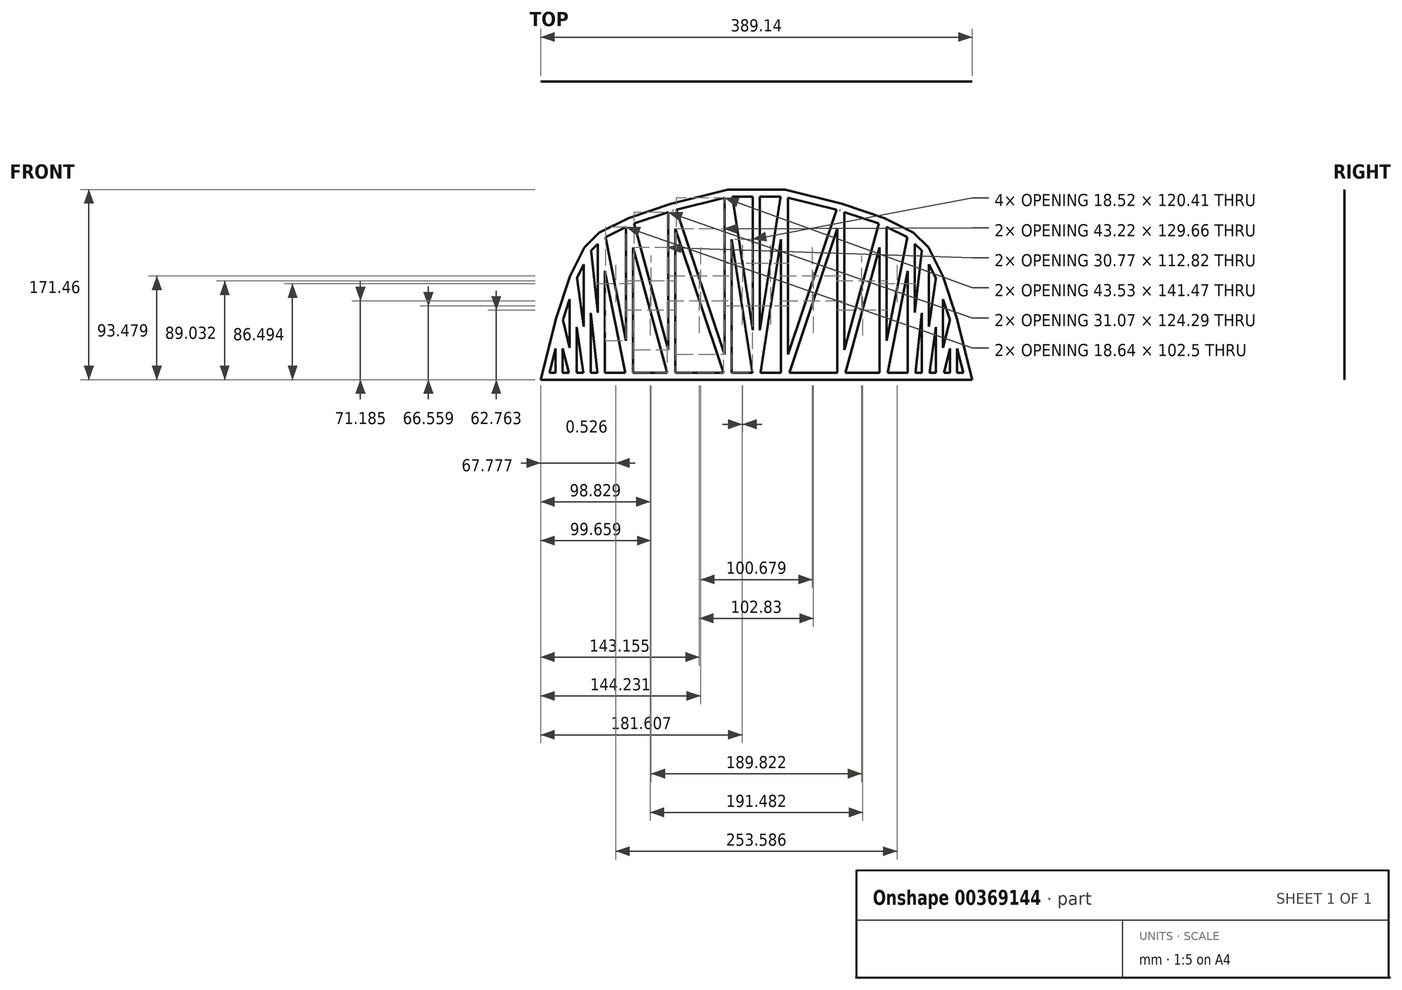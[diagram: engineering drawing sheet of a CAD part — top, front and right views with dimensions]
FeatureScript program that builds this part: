
annotation { "Feature Type Name" : "Feature", "Feature Type Description" : "" }
export const myFeature = defineFeature(function(context is Context, id is Id, definition is map)
    precondition{}
    {
        {
            var Q0;
            Q0=qCreatedBy(makeId("Front.planeOp"),FACE);
            var sketch = newSketch(context, id + "F0", { "sketchPlane" : qUnion([Q0])});
            skLineSegment(sketch, "E0", {"start": v(0, 0) * mm, "end": v(0, 165.1) * mm});
            skLineSegment(sketch, "E1", {"start": v(-75.2, 149.39) * mm, "end": v(-75.2, 149.38) * mm});
            skLineSegment(sketch, "E2", {"start": v(-193.77, 0) * mm, "end": v(-180.85, 51.69) * mm});
            skLineSegment(sketch, "E3", {"start": v(-180.85, 51.69) * mm, "end": v(-168.04, 90.12) * mm});
            skLineSegment(sketch, "E4", {"start": v(-168.04, 90.12) * mm, "end": v(-155, 116.18) * mm});
            skLineSegment(sketch, "E5", {"start": v(-155, 116.18) * mm, "end": v(-141.58, 129.6) * mm});
            skLineSegment(sketch, "E6", {"start": v(-141.58, 129.6) * mm, "end": v(-119.91, 140.44) * mm});
            skLineSegment(sketch, "E7", {"start": v(-115.52, 142.64) * mm, "end": v(-77.04, 155.47) * mm});
            skLineSegment(sketch, "E8", {"start": v(-77.09, 155.45) * mm, "end": v(-30.66, 167.06) * mm});
            skLineSegment(sketch, "E9", {"start": v(-25.8, 168.28) * mm, "end": v(0, 168.28) * mm});
            skPoint(sketch, "E10", {"position": v(-180.85, 51.69) * mm});
            skPoint(sketch, "E11", {"position": v(-168.04, 90.12) * mm});
            skPoint(sketch, "E12", {"position": v(-155, 116.18) * mm});
            skPoint(sketch, "E13", {"position": v(-141.58, 129.6) * mm});
            skLineSegment(sketch, "E14", {"start": v(-119.91, 140.44) * mm, "end": v(-115.52, 142.64) * mm});
            skPoint(sketch, "E15", {"position": v(-115.52, 142.64) * mm});
            skPoint(sketch, "E16.orphan", {"position": v(-122.1, 140.44) * mm});
            skLineSegment(sketch, "E17", {"start": v(-30.66, 167.06) * mm, "end": v(-25.8, 168.28) * mm});
            skLineSegment(sketch, "E18", {"start": v(-186.43, 3.17) * mm, "end": v(-180.97, 25) * mm});
            skLineSegment(sketch, "E19", {"start": v(-174.75, 49.91) * mm, "end": v(-168.27, 69.33) * mm});
            skPoint(sketch, "E20", {"position": v(-149.8, 112.42) * mm});
            skLineSegment(sketch, "E21.trimOffspring", {"start": v(-149.08, 113.13) * mm, "end": v(-142.88, 119.33) * mm});
            skPoint(sketch, "E22", {"position": v(-162.16, 87.68) * mm});
            skLineSegment(sketch, "E23.trimOffspring", {"start": v(-162.16, 87.68) * mm, "end": v(-155.57, 100.85) * mm});
            skPoint(sketch, "E24", {"position": v(-174.75, 49.91) * mm});
            skLineSegment(sketch, "E25", {"start": v(-136.11, 125.24) * mm, "end": v(-117.48, 134.56) * mm});
            skLineSegment(sketch, "E26", {"start": v(-110.45, 137.64) * mm, "end": v(-79.38, 148) * mm});
            skLineSegment(sketch, "E27", {"start": v(-75.31, 149.35) * mm, "end": v(-75.2, 149.38) * mm});
            skLineSegment(sketch, "E28", {"start": v(-3.17, 161.93) * mm, "end": v(-21.7, 161.93) * mm});
            skPoint(sketch, "E29", {"position": v(-137.82, 124.4) * mm});
            skPoint(sketch, "E30", {"position": v(-113.08, 136.76) * mm});
            skPoint(sketch, "E31", {"position": v(-75.31, 149.35) * mm});
            skPoint(sketch, "E32", {"position": v(-25, 161.92) * mm});
            skLineSegment(sketch, "E33", {"start": v(0, 165.1) * mm, "end": v(0, 168.28) * mm});
            skLineSegment(sketch, "E34", {"start": v(-186.43, 3.17) * mm, "end": v(-180.98, 3.17) * mm});
            skLineSegment(sketch, "E35", {"start": v(0, 0) * mm, "end": v(0, -3.18) * mm});
            skLineSegment(sketch, "E36", {"start": v(0, -3.18) * mm, "end": v(-194.57, -3.18) * mm});
            skLineSegment(sketch, "E37", {"start": v(-193.77, 0) * mm, "end": v(-194.57, -3.18) * mm});
            skLineSegment(sketch, "E38", {"start": v(-180.98, 3.17) * mm, "end": v(-180.98, 25) * mm});
            skLineSegment(sketch, "E39", {"start": v(-174.63, 3.17) * mm, "end": v(-174.63, 25) * mm});
            skLineSegment(sketch, "E40", {"start": v(-168.27, 25.8) * mm, "end": v(-174.5, 50.67) * mm});
            skLineSegment(sketch, "E41", {"start": v(-169.17, 3.17) * mm, "end": v(-174.63, 25) * mm});
            skLineSegment(sketch, "E42", {"start": v(-168.27, 25.8) * mm, "end": v(-168.27, 69.33) * mm});
            skLineSegment(sketch, "E43", {"start": v(-155.57, 44.68) * mm, "end": v(-155.57, 100.85) * mm});
            skLineSegment(sketch, "E44", {"start": v(-155.57, 44.68) * mm, "end": v(-161.82, 88.37) * mm});
            skLineSegment(sketch, "E45", {"start": v(-161.93, 44.22) * mm, "end": v(-156.06, 3.17) * mm});
            skLineSegment(sketch, "E46", {"start": v(-142.88, 57.33) * mm, "end": v(-142.88, 119.33) * mm});
            skLineSegment(sketch, "E47", {"start": v(-136.53, 94.94) * mm, "end": v(-136.53, 3.17) * mm});
            skLineSegment(sketch, "E48", {"start": v(-142.87, 57.33) * mm, "end": v(-149.08, 113.13) * mm});
            skLineSegment(sketch, "E49", {"start": v(-142.88, -0.18) * mm, "end": v(-142.9, 0) * mm});
            skLineSegment(sketch, "E50", {"start": v(-117.48, 134.56) * mm, "end": v(-117.48, 32.06) * mm});
            skLineSegment(sketch, "E51", {"start": v(-111.13, 3.17) * mm, "end": v(-111.13, 116) * mm});
            skLineSegment(sketch, "E52", {"start": v(-136.11, 125.24) * mm, "end": v(-117.48, 32.06) * mm});
            skLineSegment(sketch, "E53", {"start": v(-136.52, 94.94) * mm, "end": v(-118.17, 3.17) * mm});
            skLineSegment(sketch, "E54", {"start": v(-73.03, 132.83) * mm, "end": v(-73.03, 3.17) * mm});
            skLineSegment(sketch, "E55", {"start": v(-110.45, 137.64) * mm, "end": v(-79.38, 23.7) * mm});
            skLineSegment(sketch, "E56", {"start": v(-111.13, 116) * mm, "end": v(-80.36, 3.17) * mm});
            skLineSegment(sketch, "E57", {"start": v(-22.23, 3.17) * mm, "end": v(-22.23, 123.58) * mm});
            skLineSegment(sketch, "E58", {"start": v(-28.58, 161.03) * mm, "end": v(-28.58, 19.57) * mm});
            skLineSegment(sketch, "E59", {"start": v(-72.1, 150.15) * mm, "end": v(-28.57, 19.57) * mm});
            skLineSegment(sketch, "E60", {"start": v(-29.8, 3.17) * mm, "end": v(-73.03, 132.83) * mm});
            skLineSegment(sketch, "E61", {"start": v(-3.18, 161.93) * mm, "end": v(-3.17, 41.52) * mm});
            skLineSegment(sketch, "E62", {"start": v(-3.17, 41.52) * mm, "end": v(-21.7, 161.93) * mm});
            skLineSegment(sketch, "E63", {"start": v(-22.23, 123.58) * mm, "end": v(-3.7, 3.17) * mm});
            skLineSegment(sketch, "E64.trimOffspring", {"start": v(-143.25, 3.17) * mm, "end": v(-149.23, 56.97) * mm});
            skPoint(sketch, "E65.orphan", {"position": v(-139.7, 0) * mm});
            skPoint(sketch, "E66.orphan", {"position": v(-114.3, 0) * mm});
            skPoint(sketch, "E67.orphan", {"position": v(-149, 114.02) * mm});
            skPoint(sketch, "E68.start.orphan", {"position": v(-139.7, 127) * mm});
            skPoint(sketch, "E69.start.orphan", {"position": v(-114.3, 139.7) * mm});
            skLineSegment(sketch, "E70.trimOffspring", {"start": v(-174.63, 3.17) * mm, "end": v(-169.17, 3.17) * mm});
            skLineSegment(sketch, "E71.trimOffspring", {"start": v(-161.93, 3.17) * mm, "end": v(-156.06, 3.17) * mm});
            skLineSegment(sketch, "E72.trimOffspring", {"start": v(-161.93, 44.22) * mm, "end": v(-161.93, 3.17) * mm});
            skLineSegment(sketch, "E73.trimOffspring", {"start": v(-149.23, 3.17) * mm, "end": v(-143.25, 3.17) * mm});
            skLineSegment(sketch, "E74.trimOffspring", {"start": v(-149.23, 56.97) * mm, "end": v(-149.23, 3.17) * mm});
            skLineSegment(sketch, "E75.trimOffspring", {"start": v(-79.38, 23.7) * mm, "end": v(-79.38, 148) * mm});
            skPoint(sketch, "E76.end.orphan", {"position": v(-114.3, 127) * mm});
            skLineSegment(sketch, "E77.trimOffspring", {"start": v(-72.1, 150.15) * mm, "end": v(-28.58, 161.03) * mm});
            skLineSegment(sketch, "E78.trimOffspring", {"start": v(-75.31, 149.35) * mm, "end": v(-75.2, 149.39) * mm});
            skLineSegment(sketch, "E79.trimOffspring", {"start": v(-22.23, 3.17) * mm, "end": v(-3.7, 3.17) * mm});
            skLineSegment(sketch, "E80.trimOffspring", {"start": v(-73.03, 3.17) * mm, "end": v(-29.8, 3.17) * mm});
            skLineSegment(sketch, "E81.trimOffspring", {"start": v(-111.13, 3.17) * mm, "end": v(-80.36, 3.17) * mm});
            skLineSegment(sketch, "E82.trimOffspring", {"start": v(-136.53, 3.17) * mm, "end": v(-118.17, 3.17) * mm});
            skPoint(sketch, "E83.orphan", {"position": v(0, 161.93) * mm});
            skLineSegment(sketch, "E84.MirrorCS", {"start": v(75.2, 149.39) * mm, "end": v(75.2, 149.38) * mm});
            skLineSegment(sketch, "E85.MirrorCS", {"start": v(75.31, 149.35) * mm, "end": v(75.2, 149.39) * mm});
            skLineSegment(sketch, "E86.MirrorCS", {"start": v(75.31, 149.35) * mm, "end": v(75.2, 149.38) * mm});
            skLineSegment(sketch, "E87.MirrorCS", {"start": v(142.88, -0.18) * mm, "end": v(142.9, 0) * mm});
            skLineSegment(sketch, "E88.MirrorCS", {"start": v(174.63, 3.17) * mm, "end": v(169.17, 3.17) * mm});
            skLineSegment(sketch, "E89.MirrorCS", {"start": v(119.91, 140.44) * mm, "end": v(115.52, 142.64) * mm});
            skLineSegment(sketch, "E90.MirrorCS", {"start": v(161.93, 3.17) * mm, "end": v(156.06, 3.17) * mm});
            skLineSegment(sketch, "E91.MirrorCS", {"start": v(186.43, 3.17) * mm, "end": v(180.98, 3.17) * mm});
            skLineSegment(sketch, "E92.MirrorCS", {"start": v(193.77, 0) * mm, "end": v(194.57, -3.18) * mm});
            skLineSegment(sketch, "E93.MirrorCS", {"start": v(149.23, 3.17) * mm, "end": v(143.25, 3.17) * mm});
            skLineSegment(sketch, "E94.MirrorCS", {"start": v(30.66, 167.06) * mm, "end": v(25.8, 168.28) * mm});
            skLineSegment(sketch, "E95.MirrorCS", {"start": v(155, 116.18) * mm, "end": v(141.58, 129.6) * mm});
            skLineSegment(sketch, "E96.MirrorCS", {"start": v(162.16, 87.68) * mm, "end": v(155.57, 100.85) * mm});
            skLineSegment(sketch, "E97.MirrorCS", {"start": v(149.08, 113.13) * mm, "end": v(142.88, 119.33) * mm});
            skPoint(sketch, "E98.MirrorP", {"position": v(137.82, 124.4) * mm});
            skLineSegment(sketch, "E99.MirrorCS", {"start": v(136.53, 94.94) * mm, "end": v(136.53, 3.17) * mm});
            skLineSegment(sketch, "E100.MirrorCS", {"start": v(22.23, 123.58) * mm, "end": v(3.7, 3.17) * mm});
            skLineSegment(sketch, "E101.MirrorCS", {"start": v(111.13, 3.17) * mm, "end": v(111.13, 116) * mm});
            skLineSegment(sketch, "E102.MirrorCS", {"start": v(155.57, 44.68) * mm, "end": v(161.82, 88.37) * mm});
            skLineSegment(sketch, "E103.MirrorCS", {"start": v(161.93, 44.22) * mm, "end": v(161.93, 3.17) * mm});
            skLineSegment(sketch, "E104.MirrorCS", {"start": v(29.8, 3.17) * mm, "end": v(73.03, 132.83) * mm});
            skLineSegment(sketch, "E105.MirrorCS", {"start": v(136.53, 3.17) * mm, "end": v(118.17, 3.17) * mm});
            skLineSegment(sketch, "E106.MirrorCS", {"start": v(180.98, 3.17) * mm, "end": v(180.98, 25) * mm});
            skLineSegment(sketch, "E107.MirrorCS", {"start": v(73.03, 132.83) * mm, "end": v(73.03, 3.17) * mm});
            skLineSegment(sketch, "E108.MirrorCS", {"start": v(79.38, 23.7) * mm, "end": v(79.38, 148) * mm});
            skPoint(sketch, "E109.MirrorP", {"position": v(114.3, 127) * mm});
            skPoint(sketch, "E110.MirrorP", {"position": v(155, 116.18) * mm});
            skPoint(sketch, "E111.MirrorP", {"position": v(149, 114.02) * mm});
            skPoint(sketch, "E112.MirrorP", {"position": v(149.8, 112.42) * mm});
            skPoint(sketch, "E113.MirrorP", {"position": v(174.75, 49.91) * mm});
            skLineSegment(sketch, "E114.MirrorCS", {"start": v(142.88, 57.33) * mm, "end": v(142.88, 119.33) * mm});
            skLineSegment(sketch, "E115.MirrorCS", {"start": v(3.17, 41.52) * mm, "end": v(21.7, 161.93) * mm});
            skLineSegment(sketch, "E116.MirrorCS", {"start": v(110.45, 137.64) * mm, "end": v(79.38, 148) * mm});
            skPoint(sketch, "E117.MirrorP", {"position": v(25, 161.92) * mm});
            skLineSegment(sketch, "E118.MirrorCS", {"start": v(155.57, 44.68) * mm, "end": v(155.57, 100.85) * mm});
            skLineSegment(sketch, "E119.MirrorCS", {"start": v(117.48, 134.56) * mm, "end": v(117.48, 32.06) * mm});
            skLineSegment(sketch, "E120.MirrorCS", {"start": v(72.1, 150.15) * mm, "end": v(28.57, 19.57) * mm});
            skLineSegment(sketch, "E121.MirrorCS", {"start": v(111.13, 3.17) * mm, "end": v(80.36, 3.17) * mm});
            skPoint(sketch, "E122.MirrorP", {"position": v(114.3, 139.7) * mm});
            skLineSegment(sketch, "E123.MirrorCS", {"start": v(136.52, 94.94) * mm, "end": v(118.17, 3.17) * mm});
            skLineSegment(sketch, "E124.MirrorCS", {"start": v(149.23, 56.97) * mm, "end": v(149.23, 3.17) * mm});
            skLineSegment(sketch, "E125.MirrorCS", {"start": v(169.17, 3.17) * mm, "end": v(174.63, 25) * mm});
            skLineSegment(sketch, "E126.MirrorCS", {"start": v(22.23, 3.17) * mm, "end": v(22.23, 123.58) * mm});
            skLineSegment(sketch, "E127.MirrorCS", {"start": v(22.23, 3.17) * mm, "end": v(3.7, 3.17) * mm});
            skPoint(sketch, "E128.MirrorP", {"position": v(168.04, 90.12) * mm});
            skPoint(sketch, "E129.MirrorP", {"position": v(114.3, 0) * mm});
            skPoint(sketch, "E130.MirrorP", {"position": v(122.1, 140.44) * mm});
            skLineSegment(sketch, "E131.MirrorCS", {"start": v(161.93, 44.22) * mm, "end": v(156.06, 3.17) * mm});
            skLineSegment(sketch, "E132.MirrorCS", {"start": v(3.18, 161.93) * mm, "end": v(3.17, 41.52) * mm});
            skLineSegment(sketch, "E133.MirrorCS", {"start": v(136.11, 125.24) * mm, "end": v(117.48, 134.56) * mm});
            skPoint(sketch, "E134.MirrorP", {"position": v(75.31, 149.35) * mm});
            skLineSegment(sketch, "E135.MirrorCS", {"start": v(168.27, 25.8) * mm, "end": v(168.27, 69.33) * mm});
            skLineSegment(sketch, "E136.MirrorCS", {"start": v(28.58, 161.03) * mm, "end": v(28.58, 19.57) * mm});
            skLineSegment(sketch, "E137.MirrorCS", {"start": v(73.03, 3.17) * mm, "end": v(29.8, 3.17) * mm});
            skPoint(sketch, "E138.MirrorP", {"position": v(139.7, 127) * mm});
            skPoint(sketch, "E139.MirrorP", {"position": v(180.85, 51.69) * mm});
            skLineSegment(sketch, "E140.MirrorCS", {"start": v(0, -3.18) * mm, "end": v(194.57, -3.18) * mm});
            skLineSegment(sketch, "E141.MirrorCS", {"start": v(136.11, 125.24) * mm, "end": v(117.48, 32.06) * mm});
            skLineSegment(sketch, "E142.MirrorCS", {"start": v(168.27, 25.8) * mm, "end": v(174.5, 50.67) * mm});
            skLineSegment(sketch, "E143.MirrorCS", {"start": v(111.13, 116) * mm, "end": v(80.36, 3.17) * mm});
            skPoint(sketch, "E144.MirrorP", {"position": v(162.16, 87.68) * mm});
            skLineSegment(sketch, "E145.MirrorCS", {"start": v(186.43, 3.17) * mm, "end": v(180.97, 25) * mm});
            skLineSegment(sketch, "E146.MirrorCS", {"start": v(25.8, 168.28) * mm, "end": v(0, 168.28) * mm});
            skLineSegment(sketch, "E147.MirrorCS", {"start": v(77.09, 155.45) * mm, "end": v(30.66, 167.06) * mm});
            skLineSegment(sketch, "E148.MirrorCS", {"start": v(115.52, 142.64) * mm, "end": v(77.04, 155.47) * mm});
            skLineSegment(sketch, "E149.MirrorCS", {"start": v(141.58, 129.6) * mm, "end": v(119.91, 140.44) * mm});
            skLineSegment(sketch, "E150.MirrorCS", {"start": v(168.04, 90.12) * mm, "end": v(155, 116.18) * mm});
            skPoint(sketch, "E151.MirrorP", {"position": v(139.7, 0) * mm});
            skLineSegment(sketch, "E152.MirrorCS", {"start": v(180.85, 51.69) * mm, "end": v(168.04, 90.12) * mm});
            skPoint(sketch, "E153.MirrorP", {"position": v(115.52, 142.64) * mm});
            skLineSegment(sketch, "E154.MirrorCS", {"start": v(193.77, 0) * mm, "end": v(180.85, 51.69) * mm});
            skPoint(sketch, "E155.MirrorP", {"position": v(113.08, 136.76) * mm});
            skLineSegment(sketch, "E156.MirrorCS", {"start": v(174.75, 49.91) * mm, "end": v(168.27, 69.33) * mm});
            skLineSegment(sketch, "E157.MirrorCS", {"start": v(142.87, 57.33) * mm, "end": v(149.08, 113.13) * mm});
            skLineSegment(sketch, "E158.MirrorCS", {"start": v(143.25, 3.17) * mm, "end": v(149.23, 56.97) * mm});
            skLineSegment(sketch, "E159.MirrorCS", {"start": v(3.17, 161.93) * mm, "end": v(21.7, 161.93) * mm});
            skLineSegment(sketch, "E160.MirrorCS", {"start": v(174.63, 3.17) * mm, "end": v(174.63, 25) * mm});
            skLineSegment(sketch, "E161.MirrorCS", {"start": v(110.45, 137.64) * mm, "end": v(79.38, 23.7) * mm});
            skLineSegment(sketch, "E162.MirrorCS", {"start": v(72.1, 150.15) * mm, "end": v(28.58, 161.03) * mm});
            skPoint(sketch, "E163.MirrorP", {"position": v(141.58, 129.6) * mm});
            skSolve(sketch);
        }
        {
            var Q0;
            Q0=makeQuery(id+"F0.imprint","IMPRINT",FACE,{"disambiguationData":[TD([[makeQuery(id+"F0.imprint","IMPRINT",EDGE,{"derivedFrom":sQuery(id+"F0.wireOp",EDGE,"E0")}),1.0]])]});
            var Q1;
            Q1=makeQuery(id+"F0.imprint","IMPRINT",FACE,{"disambiguationData":[TD([[makeQuery(id+"F0.imprint","IMPRINT",EDGE,{"derivedFrom":sQuery(id+"F0.wireOp",EDGE,"E0")}),-1.0]])]});
            extrude(context, id + "F1", {"entities" : qUnion([Q0, Q1]), "depth" : 0 * mm});
        }
    });
